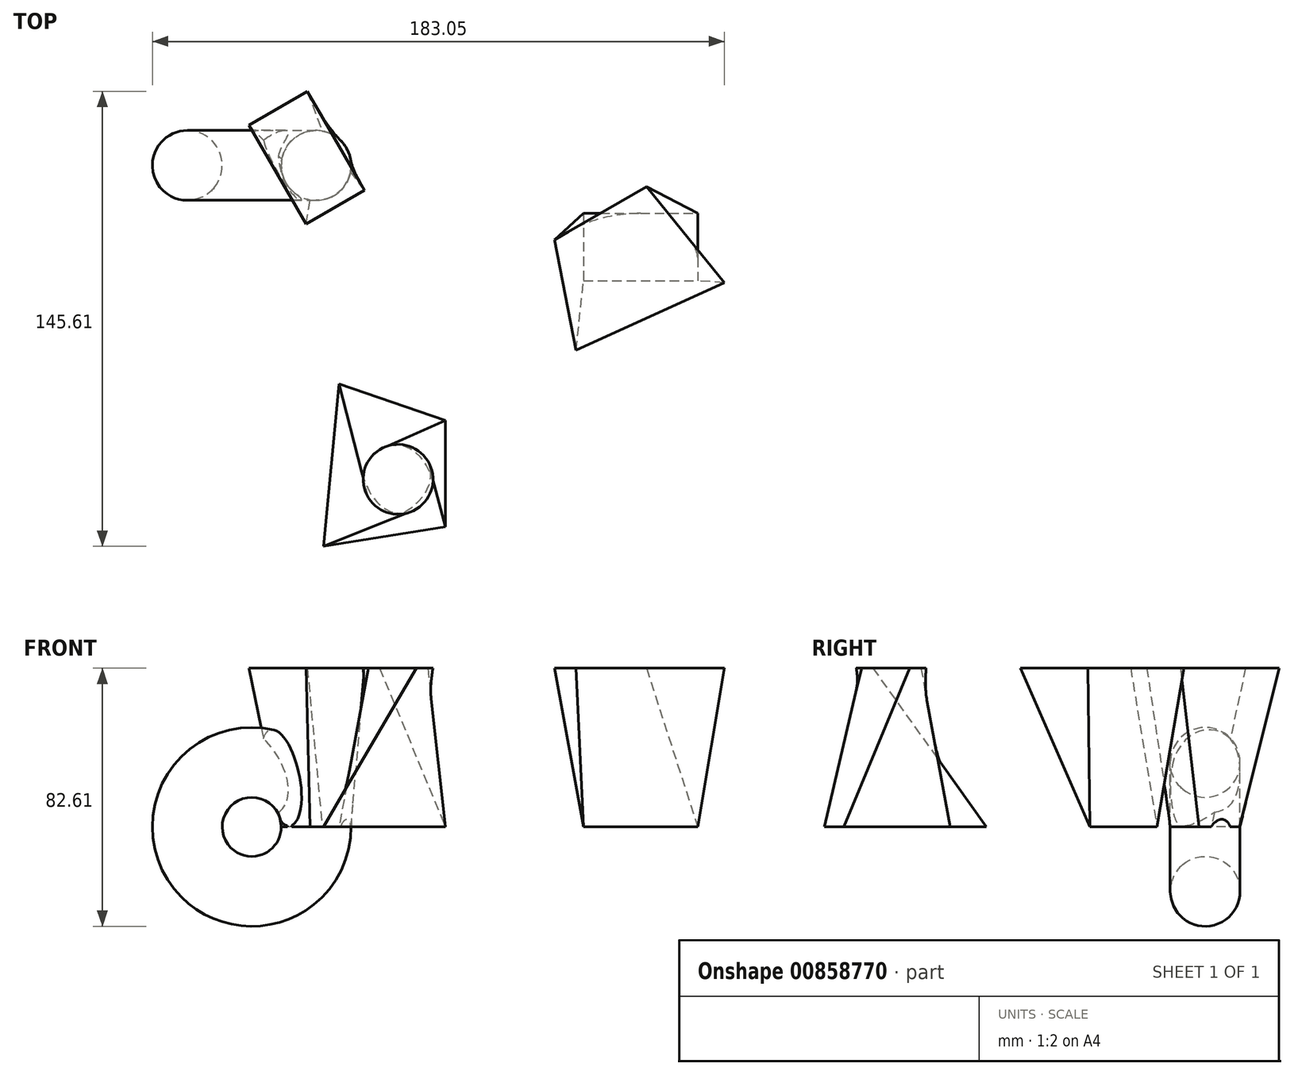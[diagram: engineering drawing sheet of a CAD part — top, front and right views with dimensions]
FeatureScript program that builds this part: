
annotation { "Feature Type Name" : "Feature", "Feature Type Description" : "" }
export const myFeature = defineFeature(function(context is Context, id is Id, definition is map)
    precondition{}
    {
        {
            var Q0;
            Q0=qCreatedBy(makeId("Top.planeOp"),FACE);
            var sketch = newSketch(context, id + "F0", { "sketchPlane" : qUnion([Q0])});
            skCircle(sketch, "E0", {"center": v(-62.28, 52.52) * mm, "radius": 11.18 * mm});
            skLineSegment(sketch, "E1.bottom", {"start": v(23.25, 37.16) * mm, "end": v(59.79, 37.16) * mm});
            skLineSegment(sketch, "E1.top", {"start": v(23.25, 15.57) * mm, "end": v(59.79, 15.57) * mm});
            skLineSegment(sketch, "E1.left", {"start": v(23.25, 37.16) * mm, "end": v(23.25, 15.57) * mm});
            skLineSegment(sketch, "E1.right", {"start": v(59.79, 37.16) * mm, "end": v(59.79, 15.57) * mm});
            skLineSegment(sketch, "E2", {"start": v(-55, -17.45) * mm, "end": v(-20.95, -29.08) * mm});
            skLineSegment(sketch, "E3", {"start": v(-20.95, -29.08) * mm, "end": v(-20.95, -63.13) * mm});
            skLineSegment(sketch, "E4", {"start": v(-20.95, -63.13) * mm, "end": v(-59.98, -69.35) * mm});
            skLineSegment(sketch, "E5", {"start": v(-59.98, -69.35) * mm, "end": v(-55, -17.45) * mm});
            skLineSegment(sketch, "E6", {"start": v(-82.91, 71.7) * mm, "end": v(-82.91, 30.26) * mm, "construction": true});
            skSolve(sketch);
        }
        {
            var Q0;
            Q0=qCreatedBy(makeId("Top.planeOp"),FACE);
            cPlane(context, id + "F1", {"entities" : qUnion([Q0]), "cplaneType" : CPlaneType.OFFSET, "offset" : 50.8 * mm, "width" : 152.4 * mm, "height" : 152.4 * mm});
        }
        {
            var Q0;
            Q0=qCreatedBy(id+"F1.planeOp",FACE);
            var sketch = newSketch(context, id + "F2", { "sketchPlane" : qUnion([Q0])});
            skCircle(sketch, "E7.0", {"center": v(-36.07, -47.94) * mm, "radius": 11.18 * mm});
            skLineSegment(sketch, "E7.1.0", {"start": v(-65.53, 33.82) * mm, "end": v(-46.83, 44.61) * mm});
            skLineSegment(sketch, "E7.1.1", {"start": v(-46.83, 44.61) * mm, "end": v(-65.1, 76.26) * mm});
            skLineSegment(sketch, "E7.1.2", {"start": v(-65.1, 76.26) * mm, "end": v(-83.8, 65.46) * mm});
            skLineSegment(sketch, "E7.1.3", {"start": v(-83.8, 65.46) * mm, "end": v(-65.53, 33.82) * mm});
            skLineSegment(sketch, "E7.2.0", {"start": v(20.9, -6.64) * mm, "end": v(68.33, 15) * mm});
            skLineSegment(sketch, "E7.2.1", {"start": v(68.33, 15) * mm, "end": v(43.42, 45.68) * mm});
            skLineSegment(sketch, "E7.2.2", {"start": v(43.42, 45.68) * mm, "end": v(13.94, 28.66) * mm});
            skLineSegment(sketch, "E7.2.3", {"start": v(13.94, 28.66) * mm, "end": v(20.9, -6.64) * mm});
            skSolve(sketch);
        }
        {
            var Q0;
            Q0=makeQuery(id+"F2.imprint","IMPRINT",FACE,{"disambiguationData":[TD([[makeQuery(id+"F2.imprint","IMPRINT",EDGE,{"derivedFrom":sQuery(id+"F2.wireOp",EDGE,"E7.0")}),1.0]])]});
            var Q1;
            Q1=makeQuery(id+"F0.imprint","IMPRINT",FACE,{"disambiguationData":[TD([[makeQuery(id+"F0.imprint","IMPRINT",EDGE,{"derivedFrom":sQuery(id+"F0.wireOp",EDGE,"E2")}),-1.0]])]});
            loft(context, id + "F3", {"sheetProfilesArray" : [{ "sheetProfileEntities" : qUnion([Q0]) }, { "sheetProfileEntities" : qUnion([Q1]) }]});
        }
        {
            var Q0;
            Q0=makeQuery(id+"F2.imprint","IMPRINT",FACE,{"disambiguationData":[TD([[makeQuery(id+"F2.imprint","IMPRINT",EDGE,{"derivedFrom":sQuery(id+"F2.wireOp",EDGE,"E7.1.0")}),1.0]])]});
            var Q1;
            Q1=makeQuery(id+"F0.imprint","IMPRINT",FACE,{"disambiguationData":[TD([[makeQuery(id+"F0.imprint","IMPRINT",EDGE,{"derivedFrom":sQuery(id+"F0.wireOp",EDGE,"E0")}),1.0]])]});
            loft(context, id + "F4", {"sheetProfilesArray" : [{ "sheetProfileEntities" : qUnion([Q0]) }, { "sheetProfileEntities" : qUnion([Q1]) }]});
        }
        {
            var Q0;
            Q0=makeQuery(id+"F2.imprint","IMPRINT",FACE,{"disambiguationData":[TD([[makeQuery(id+"F2.imprint","IMPRINT",EDGE,{"derivedFrom":sQuery(id+"F2.wireOp",EDGE,"E7.2.0")}),1.0]])]});
            var Q1;
            Q1=makeQuery(id+"F0.imprint","IMPRINT",FACE,{"disambiguationData":[TD([[makeQuery(id+"F0.imprint","IMPRINT",EDGE,{"derivedFrom":sQuery(id+"F0.wireOp",EDGE,"E1.bottom")}),-1.0]])]});
            loft(context, id + "F5", {"sheetProfilesArray" : [{ "sheetProfileEntities" : qUnion([Q0]) }, { "sheetProfileEntities" : qUnion([Q1]) }]});
        }
        {
            var Q0;
            Q0=makeQuery(id+"F0.imprint","IMPRINT",FACE,{"disambiguationData":[TD([[makeQuery(id+"F0.imprint","IMPRINT",EDGE,{"derivedFrom":sQuery(id+"F0.wireOp",EDGE,"E0")}),1.0]])]});
            var Q1;
            Q1=sQuery(id+"F0.wireOp",EDGE,"E6");
            revolve(context, id + "F6", {"operationType" : NewBodyOperationType.ADD, "surfaceOperationType" : NewSurfaceOperationType.NEW, "entities" : qUnion([Q0]), "axis" : qUnion([Q1]), "revolveType" : RevolveType.FULL});
        }
    });
